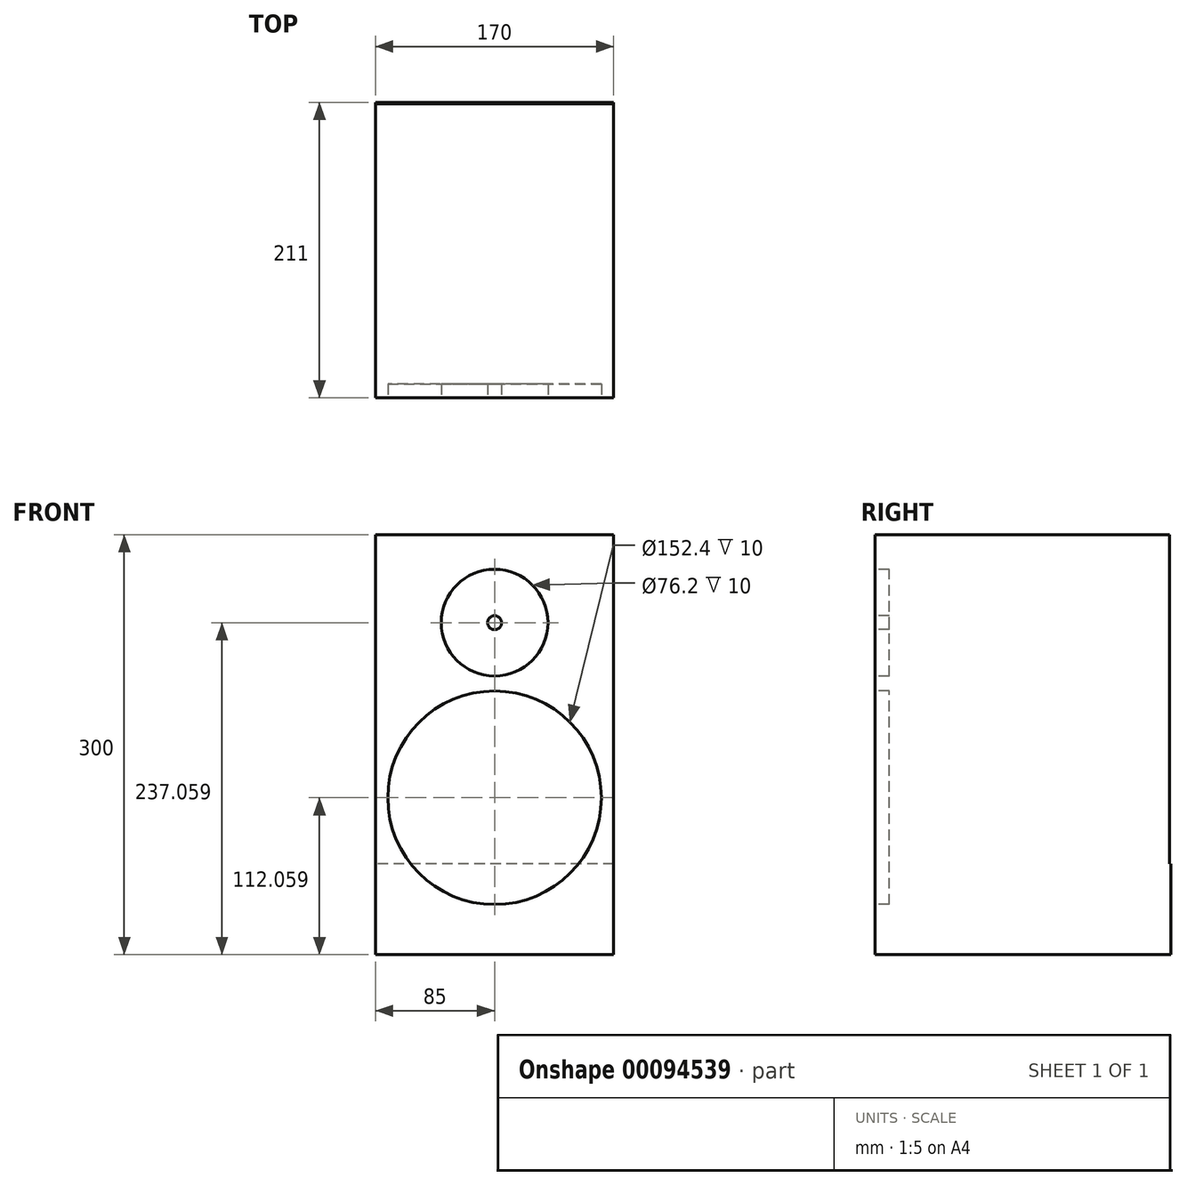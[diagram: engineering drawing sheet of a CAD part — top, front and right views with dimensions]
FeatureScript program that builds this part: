
annotation { "Feature Type Name" : "Feature", "Feature Type Description" : "" }
export const myFeature = defineFeature(function(context is Context, id is Id, definition is map)
    precondition{}
    {
        {
            var Q0;
            Q0=qCreatedBy(makeId("Top.planeOp"),FACE);
            var sketch = newSketch(context, id + "F0", { "sketchPlane" : qUnion([Q0])});
            skLineSegment(sketch, "E0.bottom", {"start": v(85, 105) * mm, "end": v(-85, 105) * mm});
            skLineSegment(sketch, "E0.top", {"start": v(85, -105) * mm, "end": v(-85, -105) * mm});
            skLineSegment(sketch, "E0.left", {"start": v(85, 105) * mm, "end": v(85, -105) * mm});
            skLineSegment(sketch, "E0.right", {"start": v(-85, 105) * mm, "end": v(-85, -105) * mm});
            skPoint(sketch, "E0.middle", {"position": v(0, 0) * mm});
            skSolve(sketch);
        }
        {
            var Q0;
            Q0 = qSketchRegion(id + "F0", true);
            var Q1;
            Q1=makeQuery(id+"F0.imprint","IMPRINT",FACE,{"disambiguationData":[TD([[makeQuery(id+"F0.imprint","IMPRINT",EDGE,{"derivedFrom":sQuery(id+"F0.wireOp",EDGE,"E0.bottom")}),1.0]])]});
            extrude(context, id + "F1", {"entities" : qUnion([Q0, Q1]), "depth" : 300 * mm});
        }
        {
            var Q0;
            Q0=makeQuery(id+"F1.opExtrude","SWEPT_FACE",FACE,{"disambiguationData":[OSD([sQuery(id+"F0.wireOp",EDGE,"E0.bottom")])]});
            var sketch = newSketch(context, id + "F2", { "sketchPlane" : qUnion([Q0])});
            skLineSegment(sketch, "E1.0", {"start": v(-85, 65) * mm, "end": v(85, 65) * mm});
            skSolve(sketch);
        }
        {
            var Q0;
            {var subQ0=sQuery(id+"F2.wireOp",EDGE,"E1.0");Q0=makeQuery(id+"F2.imprint","IMPRINT",FACE,{"disambiguationData":[TD([[makeQuery(id+"F2.imprint","IMPRINT",EDGE,{"derivedFrom":subQ0}),-1.0]])]});}
            extrude(context, id + "F3", {"entities" : qUnion([Q0]), "operationType" : NewBodyOperationType.ADD, "depth" : 1 * mm});
        }
        {
            var Q0;
            Q0=makeQuery(id+"F1.opExtrude","SWEPT_FACE",FACE,{"disambiguationData":[OSD([sQuery(id+"F0.wireOp",EDGE,"E0.top")])]});
            var sketch = newSketch(context, id + "F4", { "sketchPlane" : qUnion([Q0])});
            skLineSegment(sketch, "E2", {"start": v(0, 300) * mm, "end": v(0, 0) * mm, "construction": true});
            skCircle(sketch, "E3", {"center": v(0, 112.06) * mm, "radius": 76.2 * mm});
            skCircle(sketch, "E4", {"center": v(0, 237.06) * mm, "radius": 38.1 * mm});
            skCircle(sketch, "E5", {"center": v(0, 237.06) * mm, "radius": 5 * mm});
            skSolve(sketch);
        }
        {
            var Q0;
            Q0=makeQuery(id+"F4.imprint","IMPRINT",FACE,{"disambiguationData":[TD([[makeQuery(id+"F4.imprint","IMPRINT",EDGE,{"derivedFrom":sQuery(id+"F4.wireOp",EDGE,"E4")}),1.0]])]});
            var Q1;
            Q1=makeQuery(id+"F4.imprint","IMPRINT",FACE,{"disambiguationData":[TD([[makeQuery(id+"F4.imprint","IMPRINT",EDGE,{"derivedFrom":sQuery(id+"F4.wireOp",EDGE,"E3")}),1.0]])]});
            extrude(context, id + "F5", {"entities" : qUnion([Q0, Q1]), "operationType" : NewBodyOperationType.REMOVE, "oppositeDirection" : true, "depth" : 10 * mm});
        }
    });
